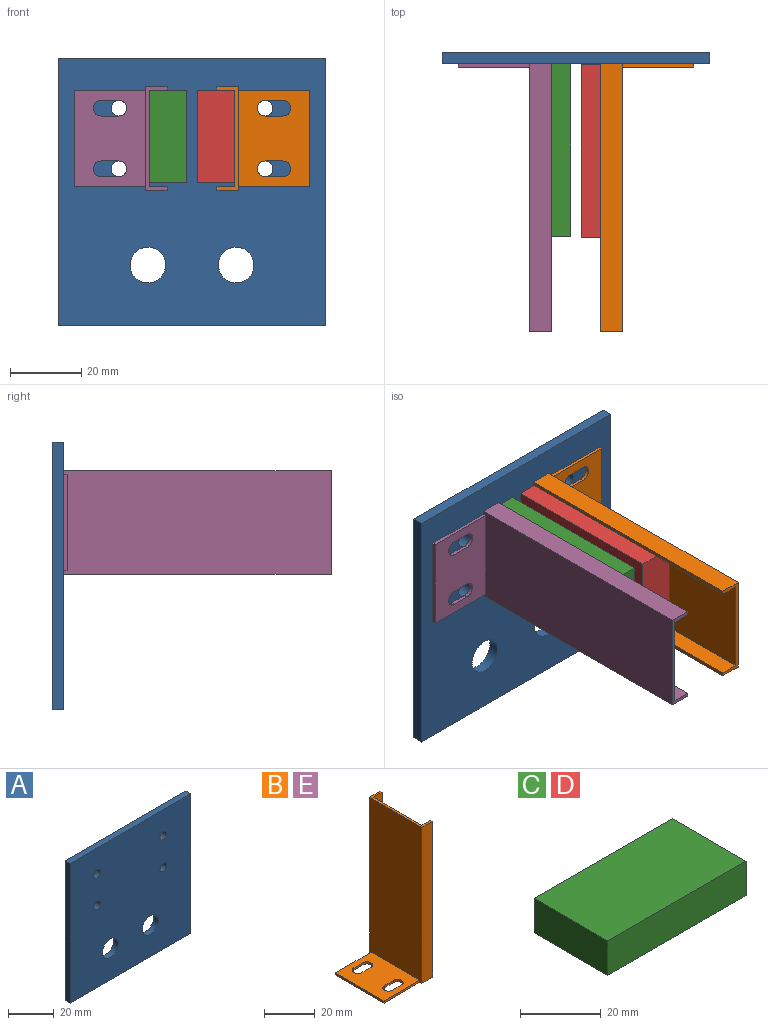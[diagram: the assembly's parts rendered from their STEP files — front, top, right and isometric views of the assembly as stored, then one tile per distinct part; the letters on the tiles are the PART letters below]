
ASSEMBLY  parts=5 mates=11
PART A: 12 faces, bbox 75x3x75 mm
  f0: plane 75x3mm, normal (-1,0,0), area 225mm2, adj f1,f8,f10,f11
  f1: plane 75x3mm, normal (0,0,-1), area 225mm2, adj f0,f2,f10,f11
  f2: plane 75x3mm, normal (1,0,0), area 225mm2, adj f1,f8,f10,f11
  f3: cylinder r=2.2mm len=4.4mm, axis (0,1,0), area 41.5mm2, adj f10,f11
  f4: cylinder r=2.2mm len=4.4mm, axis (0,1,0), area 41.5mm2, adj f10,f11
  f5: cylinder r=2.2mm len=4.4mm, axis (0,1,0), area 41.5mm2, adj f10,f11
  f6: cylinder r=5mm len=10mm, axis (0,1,0), area 94.2mm2, adj f10,f11
  f7: cylinder r=5mm len=10mm, axis (0,1,0), area 94.2mm2, adj f10,f11
  f8: plane 75x3mm, normal (0,0,1), area 225mm2, adj f0,f2,f10,f11
  f9: cylinder r=2.2mm len=4.4mm, axis (0,1,0), area 41.5mm2, adj f10,f11
  f10: plane 75x75mm, normal (0,-1,0), area 5407.1mm2, adj f0,f1,f2,f3,f4,f5,f6,f7
  f11: plane 75x75mm, normal (0,1,0), area 5407.1mm2, adj f0,f1,f2,f3,f4,f5,f6,f7
PART B: 22 faces, bbox 26x29x75 mm
  f0: cylinder r=2.2mm len=4.4mm, axis (0,0,-1), area 6.9mm2, adj f1,f10,f11,f12
  f1: plane 5x1mm, normal (0,-1,0), area 5mm2, adj f0,f2,f11,f12
  f2: cylinder r=2.2mm len=4.4mm, axis (0,0,-1), area 6.9mm2, adj f1,f10,f11,f12
  f3: cylinder r=2.2mm len=4.4mm, axis (0,0,-1), area 6.9mm2, adj f4,f8,f11,f12
  f4: plane 5x1mm, normal (0,-1,0), area 5mm2, adj f3,f5,f11,f12
  f5: cylinder r=2.2mm len=4.4mm, axis (0,0,-1), area 6.9mm2, adj f4,f8,f11,f12
  f6: plane 27x1mm, normal (-1,0,0), area 27mm2, adj f7,f9,f11,f12
  f7: plane 20x1mm, normal (0,-1,0), area 20mm2, adj f6,f11,f12,f13
  f8: plane 5x1mm, normal (0,1,0), area 5mm2, adj f3,f5,f11,f12
  f9: plane 20x1mm, normal (0,1,0), area 20mm2, adj f6,f11,f12,f13
  f10: plane 5x1mm, normal (0,1,0), area 5mm2, adj f0,f2,f11,f12
  f11: plane 27x20mm, normal (0,0,1), area 465.6mm2, adj f0,f1,f2,f3,f4,f5,f6,f7
  f12: plane 29x26mm, normal (0,0,-1), area 504.6mm2, adj f0,f1,f2,f3,f4,f5,f6,f7
  f13: plane 75x29mm, normal (-1,0,0), area 2148mm2, adj f7,f9,f11,f12,f14,f20,f21
  f14: plane 75x6mm, normal (0,1,0), area 450mm2, adj f12,f13,f15,f21
  f15: plane 75x1mm, normal (1,0,0), area 75mm2, adj f12,f14,f16,f21
  f16: plane 75x5mm, normal (0,-1,0), area 375mm2, adj f12,f15,f17,f21
  f17: plane 75x27mm, normal (1,0,0), area 2025mm2, adj f12,f16,f18,f21
  f18: plane 75x5mm, normal (0,1,0), area 375mm2, adj f12,f17,f19,f21
  f19: plane 75x1mm, normal (1,0,0), area 75mm2, adj f12,f18,f20,f21
  f20: plane 75x6mm, normal (0,-1,0), area 450mm2, adj f12,f13,f19,f21
  f21: plane 29x6mm, normal (0,0,1), area 39mm2, adj f13,f14,f15,f16,f17,f18,f19,f20
PART C: 6 faces, bbox 48.5x26x10.5 mm
  f0: plane 25.95x10.5mm, normal (-1,0,0), area 272.5mm2, adj f1,f3,f4,f5
  f1: plane 48.5x10.5mm, normal (0,-1,0), area 509.3mm2, adj f0,f2,f4,f5
  f2: plane 25.95x10.5mm, normal (1,0,0), area 272.5mm2, adj f1,f3,f4,f5
  f3: plane 48.5x10.5mm, normal (0,1,0), area 509.3mm2, adj f0,f2,f4,f5
  f4: plane 48.5x25.95mm, normal (0,0,1), area 1258.6mm2, adj f0,f1,f2,f3
  f5: plane 48.5x25.95mm, normal (0,0,-1), area 1258.6mm2, adj f0,f1,f2,f3
PART D: same geometry as C
PART E: same geometry as B
PLACE A t=(-9.68,29.72,-16.96)mm fixed
PLACE B rot(axis=(0,-0.71,0.71),180deg) t=(60.82,26.72,49.04)mm
PLACE C rot(axis=(-0.58,-0.58,0.58),120deg) t=(26.32,-21.78,49.04)mm
PLACE D rot(axis=(-0.58,0.58,-0.58),120deg) t=(29.32,26.45,49.04)mm
PLACE E rot(axis=(1,0,0),90deg) t=(-5.18,26.72,22.04)mm
MATE planar D.f4 <-> B.f17  axis (1,0,0) through (39.82,2.2,36.06)mm
MATE cylindrical A.f3 <-> B.f5  axis (0,1,0) through (48.32,26.72,44.04)mm
MATE planar B.f12 <-> A.f10  axis (0,1,0) through (49.95,26.72,35.54)mm
MATE planar C.f2 <-> A.f10  axis (0,1,0) through (21.07,26.72,36.06)mm
MATE cylindrical E.f2 <-> A.f5  axis (0,-1,0) through (7.32,25.72,44.04)mm
MATE planar D.f1 <-> B.f18  axis (0,0,1) through (34.57,2.2,49.04)mm
MATE parallel E.f14 <-> A.f8  axis (0,0,1) through (17.82,-10.78,50.04)mm
MATE parallel B.f13 <-> A.f2  axis (1,0,0) through (40.82,-11.24,35.54)mm
MATE planar C.f1 <-> E.f16  axis (0,0,1) through (26.32,2.47,49.04)mm
MATE planar C.f4 <-> E.f17  axis (-1,0,0) through (15.82,2.47,23.09)mm
MATE planar E.f12 <-> A.f10  axis (0,1,0) through (14.82,26.72,22.04)mm
